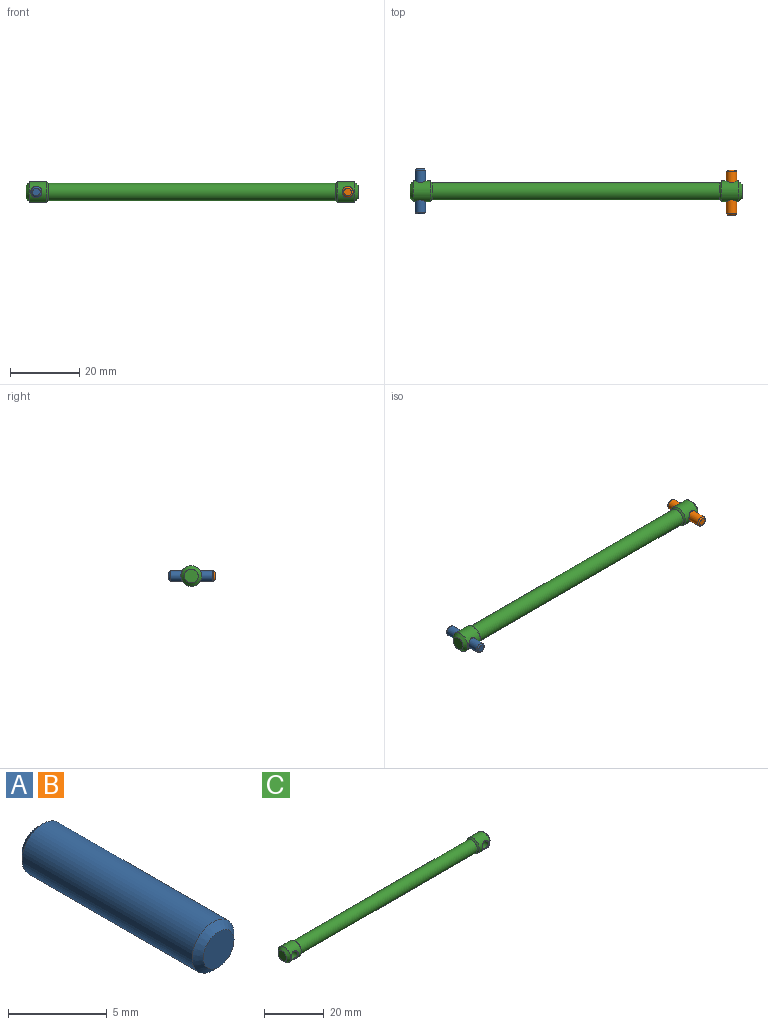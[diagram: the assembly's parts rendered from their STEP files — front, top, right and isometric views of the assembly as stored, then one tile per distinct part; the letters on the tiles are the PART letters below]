
ASSEMBLY  parts=3 mates=2
PART A: 5 faces, bbox 3x13x3 mm
  f0: cylinder r=1.5mm len=12.2mm, axis (0,1,0), area 115mm2, adj f3,f4
  f1: plane 2.2x2.2mm, normal (0,-1,0), area 3.8mm2, adj f4
  f2: plane 2.2x2.2mm, normal (0,1,0), area 3.8mm2, adj f3
  f3: cone r=1.5mm half-angle=45deg, axis (0,-1,0), area 4.6mm2, adj f0,f2
  f4: cone r=1.1mm half-angle=45deg, axis (0,1,0), area 4.6mm2, adj f0,f1
PART B: same geometry as A
PART C: 15 faces, bbox 96x6x6 mm
  f0: cylinder r=3mm len=6mm, axis (-1,0,0), area 76.4mm2, adj f4,f5,f6,f7
  f1: plane 4x4mm, normal (1,0,0), area 12.6mm2, adj f6
  f2: cylinder r=2.5mm len=83mm, axis (1,0,0), area 1303.8mm2, adj f7,f14
  f3: cylinder r=1.5mm len=4.78mm, axis (0,-1,0), area 45mm2, adj f4,f5
  f4: bspline ~3.36x3.23mm, area 1.9mm2, adj f0,f3
  f5: bspline ~3.36x3.23mm, area 1.9mm2, adj f0,f3
  f6: cone r=2mm half-angle=45deg, axis (-1,0,0), area 22.2mm2, adj f0,f1
  f7: cone r=2.5mm half-angle=45deg, axis (1,0,0), area 12.2mm2, adj f0,f2
  f8: cylinder r=3mm len=6mm, axis (1,0,0), area 76.4mm2, adj f11,f12,f13,f14
  f9: plane 4x4mm, normal (-1,0,0), area 12.6mm2, adj f13
  f10: cylinder r=1.5mm len=4.78mm, axis (0,-1,0), area 45mm2, adj f11,f12
  f11: bspline ~3.36x3.23mm, area 1.9mm2, adj f8,f10
  f12: bspline ~3.36x3.23mm, area 1.9mm2, adj f8,f10
  f13: cone r=2mm half-angle=45deg, axis (1,0,0), area 22.2mm2, adj f8,f9
  f14: cone r=2.5mm half-angle=45deg, axis (-1,0,0), area 12.2mm2, adj f2,f8
PLACE A t=(-89,0,0)mm
PLACE B t=(1,-0.4,0)mm
PLACE C t=(1,0,0)mm
MATE revolute C.f10 <-> A.f0  axis (0,-1,0) through (-89,0,0)mm
MATE revolute B.f0 <-> C.f3  axis (0,1,0) through (1,-6.5,0)mm
